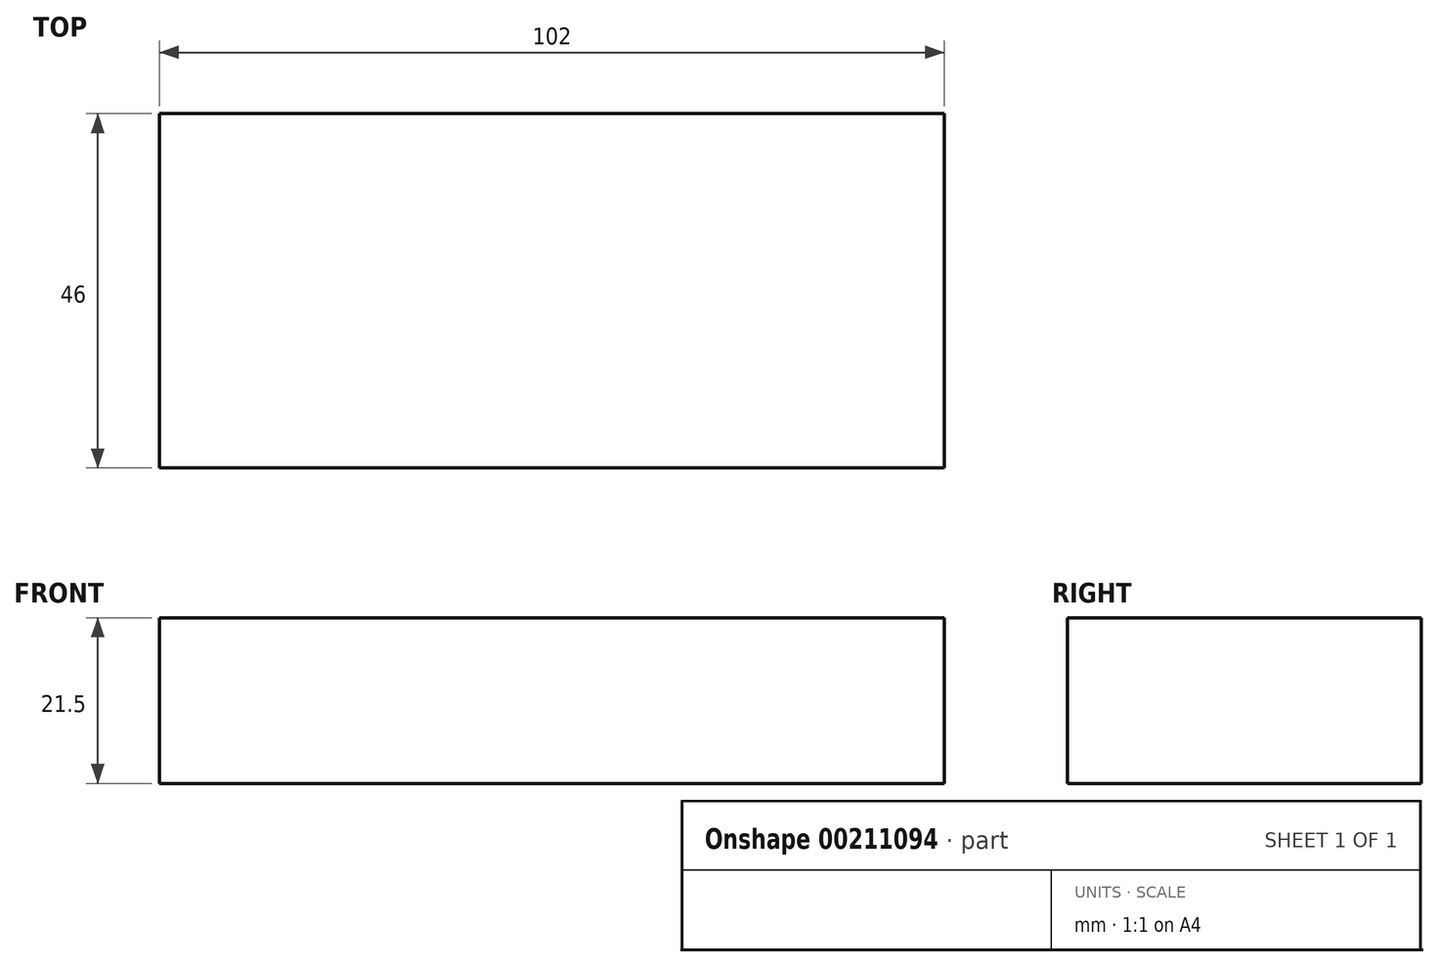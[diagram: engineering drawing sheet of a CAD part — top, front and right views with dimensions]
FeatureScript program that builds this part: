
annotation { "Feature Type Name" : "Feature", "Feature Type Description" : "" }
export const myFeature = defineFeature(function(context is Context, id is Id, definition is map)
    precondition{}
    {
        {
            var Q0;
            Q0=qCreatedBy(makeId("Top.planeOp"),FACE);
            var sketch = newSketch(context, id + "F0", { "sketchPlane" : qUnion([Q0])});
            skLineSegment(sketch, "E0.bottom", {"start": v(-121.93, 67.64) * mm, "end": v(-19.93, 67.64) * mm});
            skLineSegment(sketch, "E0.top", {"start": v(-121.93, 21.64) * mm, "end": v(-19.93, 21.64) * mm});
            skLineSegment(sketch, "E0.left", {"start": v(-121.93, 67.64) * mm, "end": v(-121.93, 21.64) * mm});
            skLineSegment(sketch, "E0.right", {"start": v(-19.93, 67.64) * mm, "end": v(-19.93, 21.64) * mm});
            skSolve(sketch);
        }
        {
            var Q0;
            Q0 = qSketchRegion(id + "F0", true);
            extrude(context, id + "F1", {"entities" : qUnion([Q0]), "depth" : 21.5 * mm});
        }
    });
